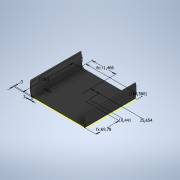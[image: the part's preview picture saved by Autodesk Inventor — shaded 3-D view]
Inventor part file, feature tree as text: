
AUTODESK INVENTOR PART (.ipt)
format: ipt  version: 2021 (Build 250183000, 183)  size: 432,640 bytes
history: native  units: mm
features: other x5, sketch x1, reference x1
ambient origin geometry x8: Origin, YZ Plane, XZ Plane, XY Plane, X Axis, Y Axis, Z Axis, Center Point
bodies: Solid1 (feature_tree), Volumenkörper1 (feature_tree)
feature tree (7):
  sketch  "Sketch1"  dims[d0=0.0mm d1=3.0mm d2=3.0mm d3=10.440924mm d4=69.779538mm d5=150.0mm d6=25.654376mm d7=168.586321mm d8=71.465973mm]
  reference  "Reference1"
  other  "<userpath>\Google Drive\Unicorn 2020\CAD_V2\Main_Assembly.iam"
  other  "Main_Assembly.iam"
  other  "Front_Panel_Assembly:1"
  other  "Front_Pane_Basel_Assembly:1"
  other  "DI 1600:1"
